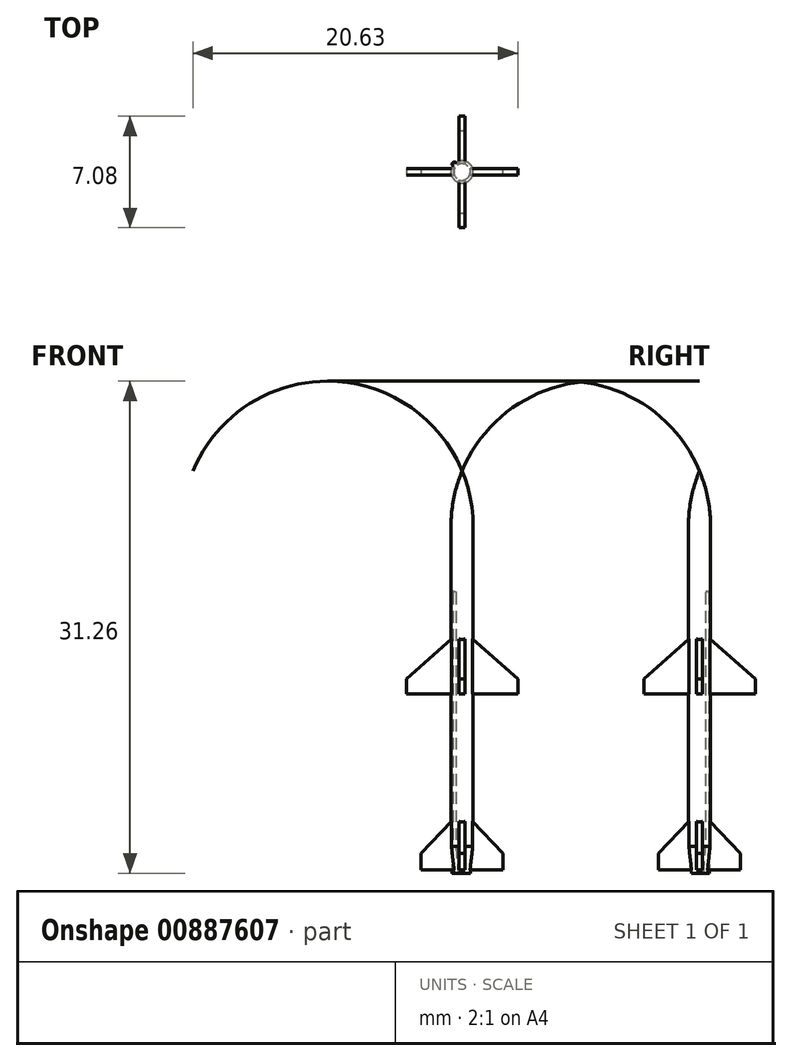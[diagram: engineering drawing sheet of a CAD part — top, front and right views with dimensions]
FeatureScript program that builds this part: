
annotation { "Feature Type Name" : "Feature", "Feature Type Description" : "" }
export const myFeature = defineFeature(function(context is Context, id is Id, definition is map)
    precondition{}
    {
        {
            assignVariable(context, id + "F0", {"name" : "s", "anyValue" : 144});
        }
        {
            var Q0;
            Q0=qCreatedBy(makeId("Front.planeOp"),FACE);
            var sketch = newSketch(context, id + "F1", { "sketchPlane" : qUnion([Q0])});
            skLineSegment(sketch, "E0", {"start": v(0, 0) * mm, "end": v(0, 25.56) * mm});
            skLineSegment(sketch, "E1", {"start": v(0.7, 22.01) * mm, "end": v(0.7, 0) * mm});
            skLineSegment(sketch, "E2", {"start": v(0.7, 0) * mm, "end": v(0, 0) * mm});
            skArc(sketch, "E3", {"start": v(0.7, 22.01) * mm, "mid": v(0.53, 23.82) * mm, "end": v(0, 25.56) * mm});
            skLineSegment(sketch, "E4", {"start": v(0.52, 0) * mm, "end": v(0.7, 1.7) * mm});
            skSolve(sketch);
        }
        {
            var Q0;
            {var subQ0=sQuery(id+"F1.wireOp",EDGE,"mrwio9nY-PsAZ-Zbfy-NhIU-sYq0QVbgGXAG");Q0=makeQuery(id+"F1.imprint","IMPRINT",FACE,{"disambiguationData":[TD([[makeQuery(id+"F1.imprint","IMPRINT",EDGE,{"derivedFrom":subQ0}),-1.0]])]});}
            var Q1;
            {var subQ7=sQuery(id+"F1.wireOp",EDGE,"E0");Q1=makeQuery(id+"F1.imprint","IMPRINT",FACE,{"disambiguationData":[TD([[makeQuery(id+"F1.imprint","IMPRINT",EDGE,{"derivedFrom":subQ7}),-1.0]])]});}
            var Q2;
            Q2=sQuery(id+"F1.wireOp",EDGE,"E0");
            revolve(context, id + "F2", {"surfaceOperationType" : NewSurfaceOperationType.NEW, "entities" : qUnion([Q0, Q1]), "axis" : qUnion([Q2]), "revolveType" : RevolveType.FULL});
        }
        {
            var Q0;
            Q0=qCreatedBy(makeId("Front.planeOp"),FACE);
            var sketch = newSketch(context, id + "F3", { "sketchPlane" : qUnion([Q0])});
            skLineSegment(sketch, "E5", {"start": v(0, 0) * mm, "end": v(0, 15.48) * mm});
            skLineSegment(sketch, "E6", {"start": v(0.4, 11.39) * mm, "end": v(0.4, 3.59) * mm});
            skLineSegment(sketch, "E7", {"start": v(0.4, 3.59) * mm, "end": v(2.6, 1.25) * mm});
            skLineSegment(sketch, "E8", {"start": v(0.7, 0) * mm, "end": v(0.7, 32.87) * mm, "construction": true});
            skPoint(sketch, "E9", {"position": v(0.7, 3.26) * mm});
            skLineSegment(sketch, "E10", {"start": v(0.4, 11.39) * mm, "end": v(3.54, 11.39) * mm});
            skLineSegment(sketch, "E11", {"start": v(3.54, 11.39) * mm, "end": v(3.54, 12.36) * mm});
            skLineSegment(sketch, "E12", {"start": v(3.54, 12.36) * mm, "end": v(0, 15.48) * mm});
            skPoint(sketch, "E13", {"position": v(0.7, 11.39) * mm});
            skPoint(sketch, "E14", {"position": v(0.7, 14.86) * mm});
            skLineSegment(sketch, "E15", {"start": v(0, 0.2) * mm, "end": v(2.6, 0.2) * mm});
            skLineSegment(sketch, "E16", {"start": v(2.6, 0.2) * mm, "end": v(2.6, 1.25) * mm});
            skLineSegment(sketch, "E17.0", {"start": v(0.7, 1.7) * mm, "end": v(-0.7, 1.7) * mm});
            skSolve(sketch);
        }
        {
            var Q0;
            Q0=qSketchRegion(id+"F3",true);
            extrude(context, id + "F4", {"entities" : qUnion([Q0]), "operationType" : NewBodyOperationType.ADD, "depth" : .4 * mm, "offsetDistance" : 25 * mm, "symmetric" : true});
        }
        {
            var Q0;
            Q0=makeQuery(id+"F2.opRevolve","SWEPT_BODY",BODY,{"disambiguationData":[OSD([sQuery(id+"F1.wireOp",EDGE,"E0"),sQuery(id+"F1.wireOp",EDGE,"E1"),sQuery(id+"F1.wireOp",EDGE,"E2"),sQuery(id+"F1.wireOp",EDGE,"2EiOItwe-9FNA-eY8p-DkXH-AMy5AHyUmzZA"),sQuery(id+"F1.wireOp",EDGE,"lF35QjYl-MEgV-fRWE-0Yr6-Bt5vS8A7brRf")])]});
            var Q1;
            Q1=makeQuery(id+"F2.opRevolve","SWEPT_FACE",FACE,{"disambiguationData":[OSD([sQuery(id+"F1.wireOp",EDGE,"E1")])]});
            circularPattern(context, id + "F5", {"operationType" : NewBodyOperationType.ADD, "entities" : qUnion([Q0]), "axis" : qUnion([Q1]), "angle" : 360 * degree, "instanceCount" : 4, "equalSpace" : true, "computeTransformsWithoutBuiltin" : true});
        }
        {
            var Q0;
            Q0=makeQuery(id+"F2.opRevolve","SWEPT_FACE",FACE,{"disambiguationData":[OSD([sQuery(id+"F1.wireOp",EDGE,"E2")])]});
            var sketch = newSketch(context, id + "F6", { "sketchPlane" : qUnion([Q0])});
            skLineSegment(sketch, "E18", {"start": v(-0.06, -0.25) * mm, "end": v(-0.25, -0.06) * mm});
            skLineSegment(sketch, "E19", {"start": v(-0.25, -0.06) * mm, "end": v(-0.59, -0.4) * mm});
            skLineSegment(sketch, "E20", {"start": v(-0.4, -0.59) * mm, "end": v(-0.06, -0.25) * mm});
            skLineSegment(sketch, "E21", {"start": v(0, -0.45) * mm, "end": v(0, 0) * mm, "construction": true});
            skLineSegment(sketch, "E22", {"start": v(0, 0) * mm, "end": v(-0.16, -0.16) * mm, "construction": true});
            skArc(sketch, "E23", {"start": v(-0.59, -0.4) * mm, "mid": v(-0.59, -0.59) * mm, "end": v(-0.4, -0.59) * mm});
            skSolve(sketch);
        }
        {
            var Q0;
            Q0=qSketchRegion(id+"F6",true);
            extrude(context, id + "F7", {"entities" : qUnion([Q0]), "operationType" : NewBodyOperationType.ADD, "oppositeDirection" : true, "depth" : (2580 / getVariable(context, 's')) * mm, "offsetDistance" : 25 * mm});
        }
        {
            var Q0;
            Q0=makeQuery(id+"F7.opExtrude","CAP_EDGE",EDGE,{"disambiguationData":[OSD([sQuery(id+"F6.wireOp",EDGE,"E23")])],"isStart":false});
            fillet(context, id + "F8", {"entities" : qUnion([Q0]), "radius" : (15 / getVariable(context, 's')) * mm, "tangentPropagation" : true, "allowEdgeOverflow" : false});
        }
    });
